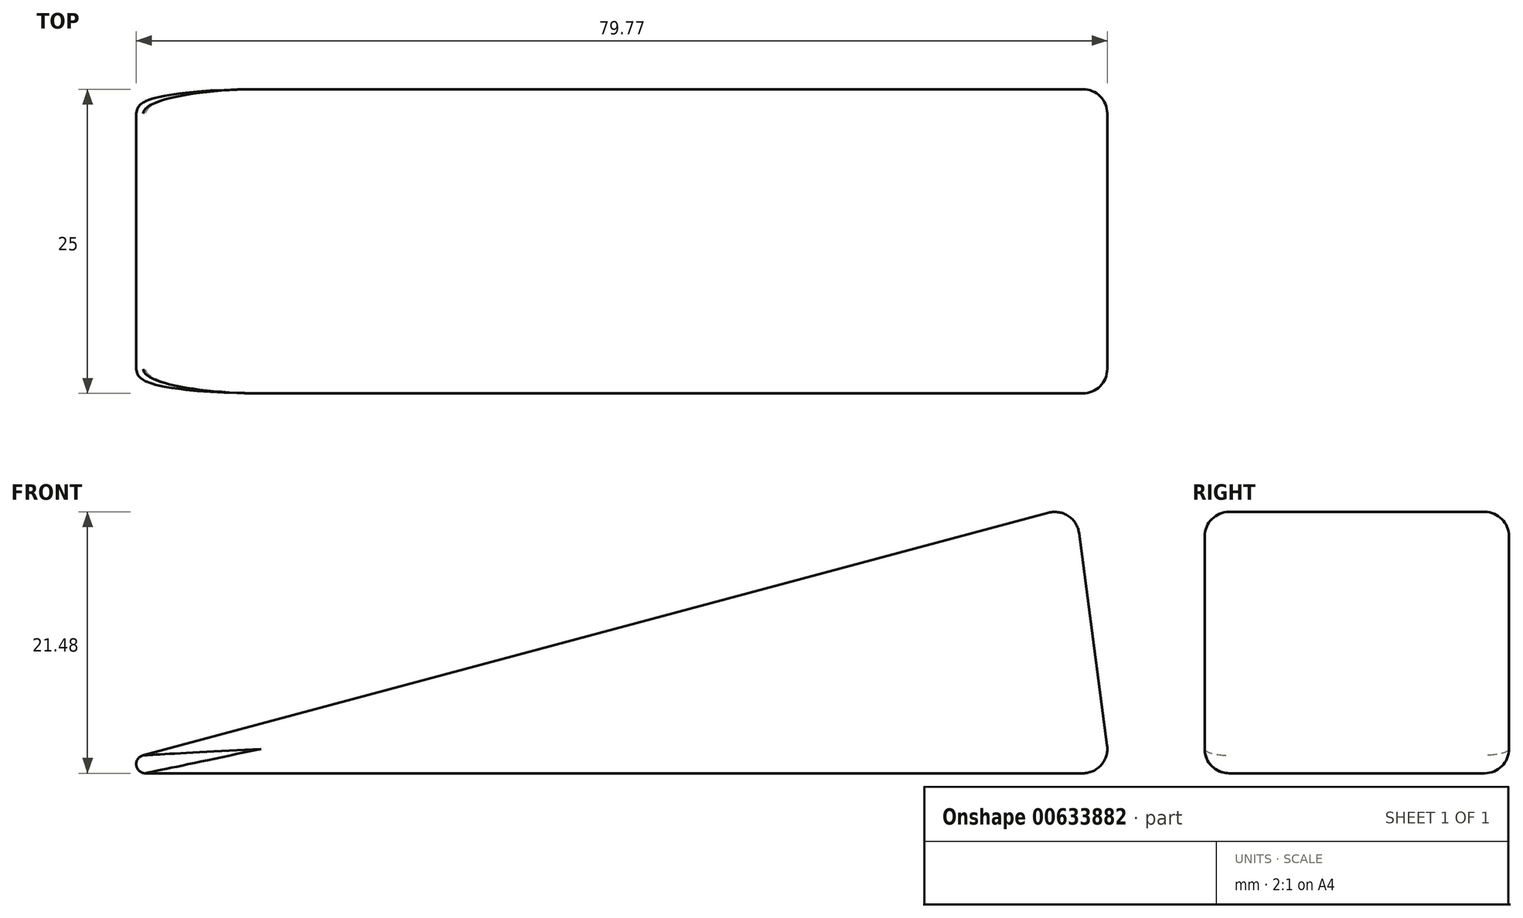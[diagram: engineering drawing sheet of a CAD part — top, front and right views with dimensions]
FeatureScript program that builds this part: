
annotation { "Feature Type Name" : "Feature", "Feature Type Description" : "" }
export const myFeature = defineFeature(function(context is Context, id is Id, definition is map)
    precondition{}
    {
        {
            var Q0;
            Q0=qCreatedBy(makeId("Front.planeOp"),FACE);
            var sketch = newSketch(context, id + "F0", { "sketchPlane" : qUnion([Q0])});
            skLineSegment(sketch, "E0", {"start": v(0, 0) * mm, "end": v(-85, 0) * mm});
            skLineSegment(sketch, "E1", {"start": v(-85, 0) * mm, "end": v(-2.9, 22) * mm});
            skLineSegment(sketch, "E2", {"start": v(-2.9, 22) * mm, "end": v(0, 0) * mm});
            skSolve(sketch);
        }
        {
            var Q0;
            Q0 = qSketchRegion(id + "F0", true);
            extrude(context, id + "F1", {"entities" : qUnion([Q0]), "depth" : 25 * mm, "offsetDistance" : 25 * mm});
        }
        {
            var Q0;
            Q0=makeQuery(id+"F1.opExtrude","SWEPT_EDGE",EDGE,{"disambiguationData":[OSD([sQuery(id+"F0.wireOp",EDGE,"E0"),sQuery(id+"F0.wireOp",EDGE,"E1")])]});
            fillet(context, id + "F2", {"entities" : qUnion([Q0]), "radius" : 0.75 * mm, "tangentPropagation" : true, "allowEdgeOverflow" : false});
        }
        {
            var Q0;
            Q0=makeQuery(id+"F1.opExtrude","SWEPT_EDGE",EDGE,{"disambiguationData":[OSD([sQuery(id+"F0.wireOp",EDGE,"E1"),sQuery(id+"F0.wireOp",EDGE,"E2")])]});
            var Q1;
            Q1=makeQuery(id+"F1.opExtrude","SWEPT_EDGE",EDGE,{"disambiguationData":[OSD([sQuery(id+"F0.wireOp",EDGE,"E0"),sQuery(id+"F0.wireOp",EDGE,"E2")])]});
            fillet(context, id + "F3", {"entities" : qUnion([Q0, Q1]), "radius" : 2 * mm, "tangentPropagation" : true, "allowEdgeOverflow" : false});
        }
        {
            var Q0;
            Q0=makeQuery(id+"F1.opExtrude","CAP_FACE",FACE,{"disambiguationData":[OSD([sQuery(id+"F0.wireOp",EDGE,"E0"),sQuery(id+"F0.wireOp",EDGE,"E1"),sQuery(id+"F0.wireOp",EDGE,"E2")])],"isStart":false});
            var Q1;
            Q1=makeQuery(id+"F1.opExtrude","CAP_FACE",FACE,{"disambiguationData":[OSD([sQuery(id+"F0.wireOp",EDGE,"E0"),sQuery(id+"F0.wireOp",EDGE,"E1"),sQuery(id+"F0.wireOp",EDGE,"E2")])],"isStart":true});
            fillet(context, id + "F4", {"entities" : qUnion([Q0, Q1]), "radius" : 2 * mm, "tangentPropagation" : true, "allowEdgeOverflow" : false});
        }
    });
